# Revit family: Door-Slider-90_Degree_Corner-Fleetwood-3070-XXXXVXXXX
name_source: partatom
category: Doors
revit_build: Autodesk Revit Architecture 2013 (Build: 20120221_2030(x64)
units: mm (PartAtom-declared; Revit-internal decimal feet)

## types (1)
- Door-Slider-90_Degree_Corner-Fleetwood-3070-XXXXVXXXX
    2nd_Wall_Thickness = 12 "
    Actuator_Height = 48 "
    Centerline_1 = 0 "
    Centerline_2 = 0 "
    Centerline_3 = 0 "
    Centerline_5 = 0 "
    Centerline_6 = 0 "
    Centerline_7 = 0 "
    Configuration = XXXXVXXXX
    Custom_Centerlines = No
    Equal_Glass_Centerlines = Yes
    Frame_and_Panel = Aluminum, Anodized Clear
    Function = Exterior
    Glazing = Glass
    Hardware = Stainless Steel, Brushed
    Height = 96 "
    Manufacturer = Fleetwood Windows and Doors
    Model = Series 3070
    Panel_1 = 44.7601 "
    Panel_2 = 42.8651 "
    Panel_3 = 42.8651 "
    Panel_4 = 44.7601 "
    Panel_5 = 46.2797 "
    Panel_6 = 42.8897 "
    Panel_7 = 42.8897 "
    Panel_8 = 44.7847 "
    Rough Height = 96.25 "
    Rough Width = 180 "
    Rough Width_2 = 180 "
    Shim_Space = 0.25 "
    Thickness = 7.632 "
    Type Comments = 90 Degree Multi-Slide Door
    Wall Closure = By host
    Wall_Thickness = 12 "
    Width = 177.566 "
    Width_2 = 177.566 "

## geometry (parser evidence)
native form markers: Blend x24, Sweep x13
no freeform markers — native parametric forms only
